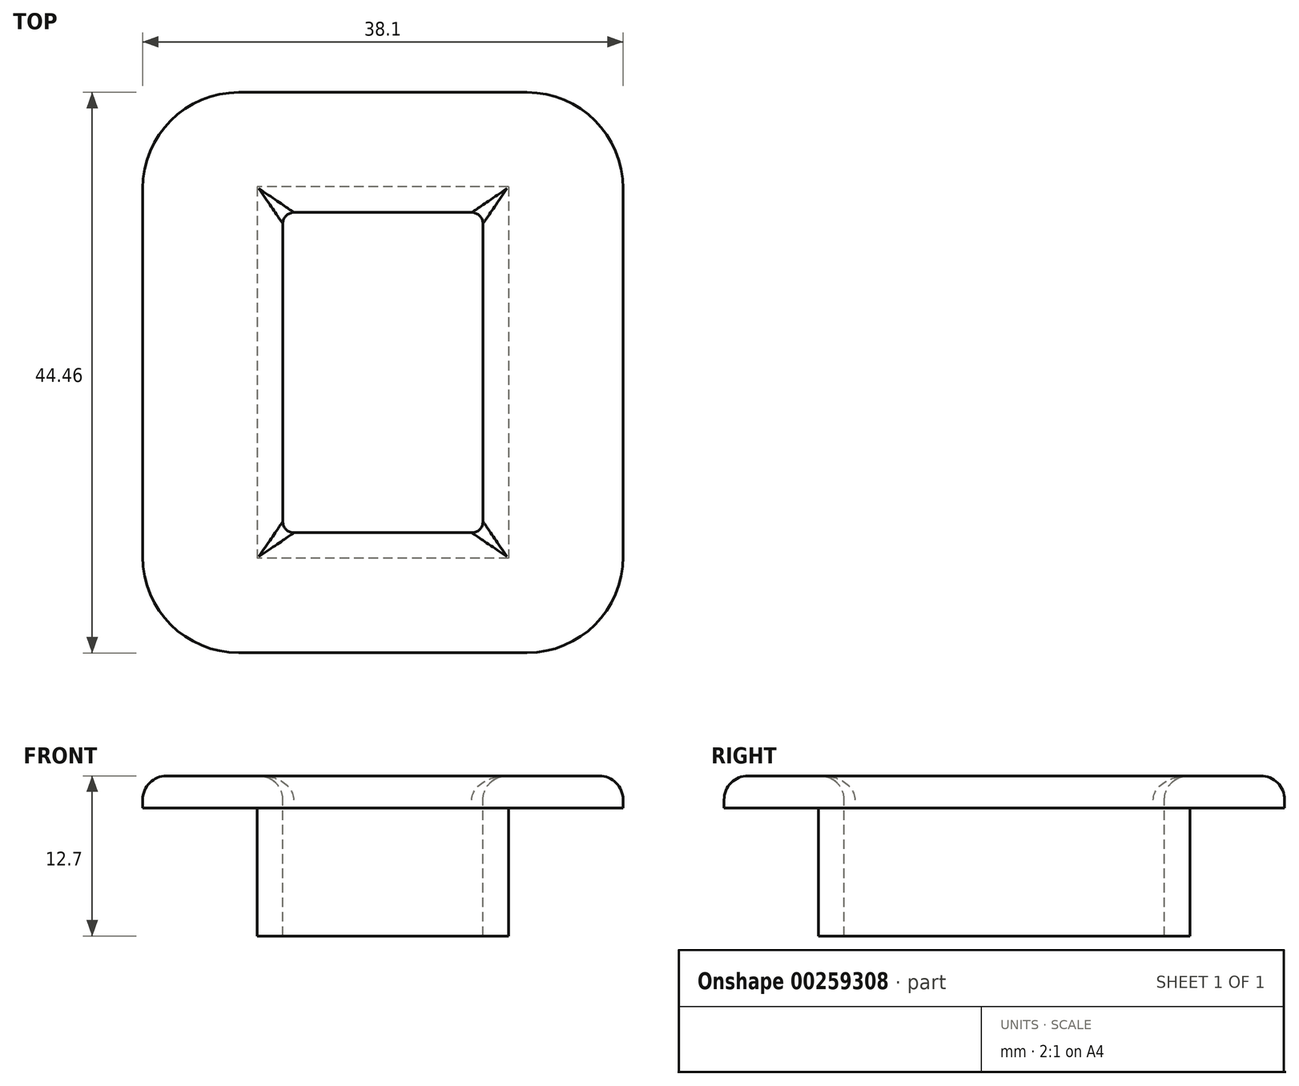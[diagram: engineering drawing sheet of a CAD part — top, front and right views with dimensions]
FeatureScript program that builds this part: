
annotation { "Feature Type Name" : "Feature", "Feature Type Description" : "" }
export const myFeature = defineFeature(function(context is Context, id is Id, definition is map)
    precondition{}
    {
        {
            var Q0;
            Q0=qCreatedBy(makeId("Top.planeOp"),FACE);
            var sketch = newSketch(context, id + "F0", { "sketchPlane" : qUnion([Q0])});
            skLineSegment(sketch, "E0.bottom", {"start": v(-7.94, 12.7) * mm, "end": v(7.94, 12.7) * mm});
            skLineSegment(sketch, "E0.top", {"start": v(-7.94, -12.7) * mm, "end": v(7.94, -12.7) * mm});
            skLineSegment(sketch, "E0.left", {"start": v(-7.94, 12.7) * mm, "end": v(-7.94, -12.7) * mm});
            skLineSegment(sketch, "E0.right", {"start": v(7.94, 12.7) * mm, "end": v(7.94, -12.7) * mm});
            skPoint(sketch, "E0.middle", {"position": v(0, 0) * mm});
            skLineSegment(sketch, "E1.bottom", {"start": v(19.05, 22.23) * mm, "end": v(-19.05, 22.23) * mm});
            skLineSegment(sketch, "E1.top", {"start": v(19.05, -22.23) * mm, "end": v(-19.05, -22.23) * mm});
            skLineSegment(sketch, "E1.left", {"start": v(19.05, 22.23) * mm, "end": v(19.05, -22.23) * mm});
            skLineSegment(sketch, "E1.right", {"start": v(-19.05, 22.23) * mm, "end": v(-19.05, -22.23) * mm});
            skSolve(sketch);
        }
        {
            var Q0;
            Q0 = qSketchRegion(id + "F0", true);
            extrude(context, id + "F1", {"entities" : qUnion([Q0]), "oppositeDirection" : true, "depth" : 12.7 * mm});
        }
        {
            var Q0;
            Q0=makeQuery(id+"F1.opExtrude","CAP_EDGE",EDGE,{"disambiguationData":[OSD([sQuery(id+"F0.wireOp",EDGE,"E0.bottom")])],"isStart":true});
            var Q1;
            Q1=makeQuery(id+"F1.opExtrude","CAP_EDGE",EDGE,{"disambiguationData":[OSD([sQuery(id+"F0.wireOp",EDGE,"E0.right")])],"isStart":true});
            var Q2;
            Q2=makeQuery(id+"F1.opExtrude","CAP_EDGE",EDGE,{"disambiguationData":[OSD([sQuery(id+"F0.wireOp",EDGE,"E0.top")])],"isStart":true});
            var Q3;
            Q3=makeQuery(id+"F1.opExtrude","CAP_EDGE",EDGE,{"disambiguationData":[OSD([sQuery(id+"F0.wireOp",EDGE,"E0.left")])],"isStart":true});
            var Q4;
            Q4=makeQuery(id+"F1.opExtrude","CAP_EDGE",EDGE,{"disambiguationData":[OSD([sQuery(id+"F0.wireOp",EDGE,"E1.right")])],"isStart":true});
            var Q5;
            Q5=makeQuery(id+"F1.opExtrude","CAP_EDGE",EDGE,{"disambiguationData":[OSD([sQuery(id+"F0.wireOp",EDGE,"E1.bottom")])],"isStart":true});
            var Q6;
            Q6=makeQuery(id+"F1.opExtrude","CAP_EDGE",EDGE,{"disambiguationData":[OSD([sQuery(id+"F0.wireOp",EDGE,"E1.left")])],"isStart":true});
            var Q7;
            Q7=makeQuery(id+"F1.opExtrude","CAP_EDGE",EDGE,{"disambiguationData":[OSD([sQuery(id+"F0.wireOp",EDGE,"E1.top")])],"isStart":true});
            fillet(context, id + "F2", {"entities" : qUnion([Q0, Q1, Q2, Q3, Q4, Q5, Q6, Q7]), "radius" : 1.9 * mm, "tangentPropagation" : true, "allowEdgeOverflow" : false});
        }
        {
            var Q0;
            Q0=makeQuery(id+"F1.opExtrude","SWEPT_EDGE",EDGE,{"disambiguationData":[OSD([sQuery(id+"F0.wireOp",EDGE,"E0.bottom"),sQuery(id+"F0.wireOp",EDGE,"E0.right")])]});
            var Q1;
            Q1=makeQuery(id+"F1.opExtrude","SWEPT_EDGE",EDGE,{"disambiguationData":[OSD([sQuery(id+"F0.wireOp",EDGE,"E0.bottom"),sQuery(id+"F0.wireOp",EDGE,"E0.left")])]});
            var Q2;
            Q2=makeQuery(id+"F1.opExtrude","SWEPT_EDGE",EDGE,{"disambiguationData":[OSD([sQuery(id+"F0.wireOp",EDGE,"E0.top"),sQuery(id+"F0.wireOp",EDGE,"E0.left")])]});
            var Q3;
            Q3=makeQuery(id+"F1.opExtrude","SWEPT_EDGE",EDGE,{"disambiguationData":[OSD([sQuery(id+"F0.wireOp",EDGE,"E0.top"),sQuery(id+"F0.wireOp",EDGE,"E0.right")])]});
            fillet(context, id + "F3", {"entities" : qUnion([Q0, Q1, Q2, Q3]), "radius" : 0.89 * mm, "allowEdgeOverflow" : false});
        }
        {
            var Q0;
            Q0=makeQuery(id+"F1.opExtrude","SWEPT_EDGE",EDGE,{"disambiguationData":[OSD([sQuery(id+"F0.wireOp",EDGE,"E1.bottom"),sQuery(id+"F0.wireOp",EDGE,"E1.right")])]});
            var Q1;
            Q1=makeQuery(id+"F1.opExtrude","SWEPT_EDGE",EDGE,{"disambiguationData":[OSD([sQuery(id+"F0.wireOp",EDGE,"E1.bottom"),sQuery(id+"F0.wireOp",EDGE,"E1.left")])]});
            var Q2;
            Q2=makeQuery(id+"F1.opExtrude","SWEPT_EDGE",EDGE,{"disambiguationData":[OSD([sQuery(id+"F0.wireOp",EDGE,"E1.top"),sQuery(id+"F0.wireOp",EDGE,"E1.right")])]});
            var Q3;
            Q3=makeQuery(id+"F1.opExtrude","SWEPT_EDGE",EDGE,{"disambiguationData":[OSD([sQuery(id+"F0.wireOp",EDGE,"E1.top"),sQuery(id+"F0.wireOp",EDGE,"E1.left")])]});
            fillet(context, id + "F4", {"entities" : qUnion([Q0, Q1, Q2, Q3]), "radius" : 7.62 * mm, "tangentPropagation" : true, "allowEdgeOverflow" : false});
        }
        {
            var Q0;
            Q0=makeQuery(id+"F1.opExtrude","CAP_FACE",FACE,{"disambiguationData":[OSD([sQuery(id+"F0.wireOp",EDGE,"E0.bottom"),sQuery(id+"F0.wireOp",EDGE,"E0.top"),sQuery(id+"F0.wireOp",EDGE,"E0.left"),sQuery(id+"F0.wireOp",EDGE,"E0.right"),sQuery(id+"F0.wireOp",EDGE,"E1.bottom"),sQuery(id+"F0.wireOp",EDGE,"E1.top"),sQuery(id+"F0.wireOp",EDGE,"E1.left"),sQuery(id+"F0.wireOp",EDGE,"E1.right")])],"isStart":false});
            var sketch = newSketch(context, id + "F5", { "sketchPlane" : qUnion([Q0])});
            skLineSegment(sketch, "E2.0", {"start": v(19.05, -14.6) * mm, "end": v(19.05, 14.6) * mm});
            skArc(sketch, "E2.1", {"start": v(19.05, 14.6) * mm, "mid": v(16.82, 20) * mm, "end": v(11.43, 22.23) * mm});
            skLineSegment(sketch, "E2.2", {"start": v(11.43, 22.23) * mm, "end": v(-11.43, 22.23) * mm});
            skArc(sketch, "E2.3", {"start": v(-11.43, 22.23) * mm, "mid": v(-16.82, 20) * mm, "end": v(-19.05, 14.6) * mm});
            skLineSegment(sketch, "E2.4", {"start": v(-19.05, -14.6) * mm, "end": v(-19.05, 14.6) * mm});
            skArc(sketch, "E2.5", {"start": v(-19.05, -14.6) * mm, "mid": v(-16.82, -20) * mm, "end": v(-11.43, -22.23) * mm});
            skLineSegment(sketch, "E2.6", {"start": v(11.43, -22.23) * mm, "end": v(-11.43, -22.23) * mm});
            skArc(sketch, "E2.7", {"start": v(11.43, -22.23) * mm, "mid": v(16.82, -20) * mm, "end": v(19.05, -14.6) * mm});
            skLineSegment(sketch, "E3.bottom", {"start": v(9.97, -14.73) * mm, "end": v(-9.97, -14.73) * mm});
            skLineSegment(sketch, "E3.top", {"start": v(9.97, 14.73) * mm, "end": v(-9.97, 14.73) * mm});
            skLineSegment(sketch, "E3.left", {"start": v(9.97, -14.73) * mm, "end": v(9.97, 14.73) * mm});
            skLineSegment(sketch, "E3.right", {"start": v(-9.97, -14.73) * mm, "end": v(-9.97, 14.73) * mm});
            skPoint(sketch, "E3.middle", {"position": v(0, 0) * mm});
            skSolve(sketch);
        }
        {
            var Q0;
            Q0 = qSketchRegion(id + "F5", true);
            extrude(context, id + "F6", {"entities" : qUnion([Q0]), "operationType" : NewBodyOperationType.REMOVE, "oppositeDirection" : true, "depth" : 10.16 * mm});
        }
    });
